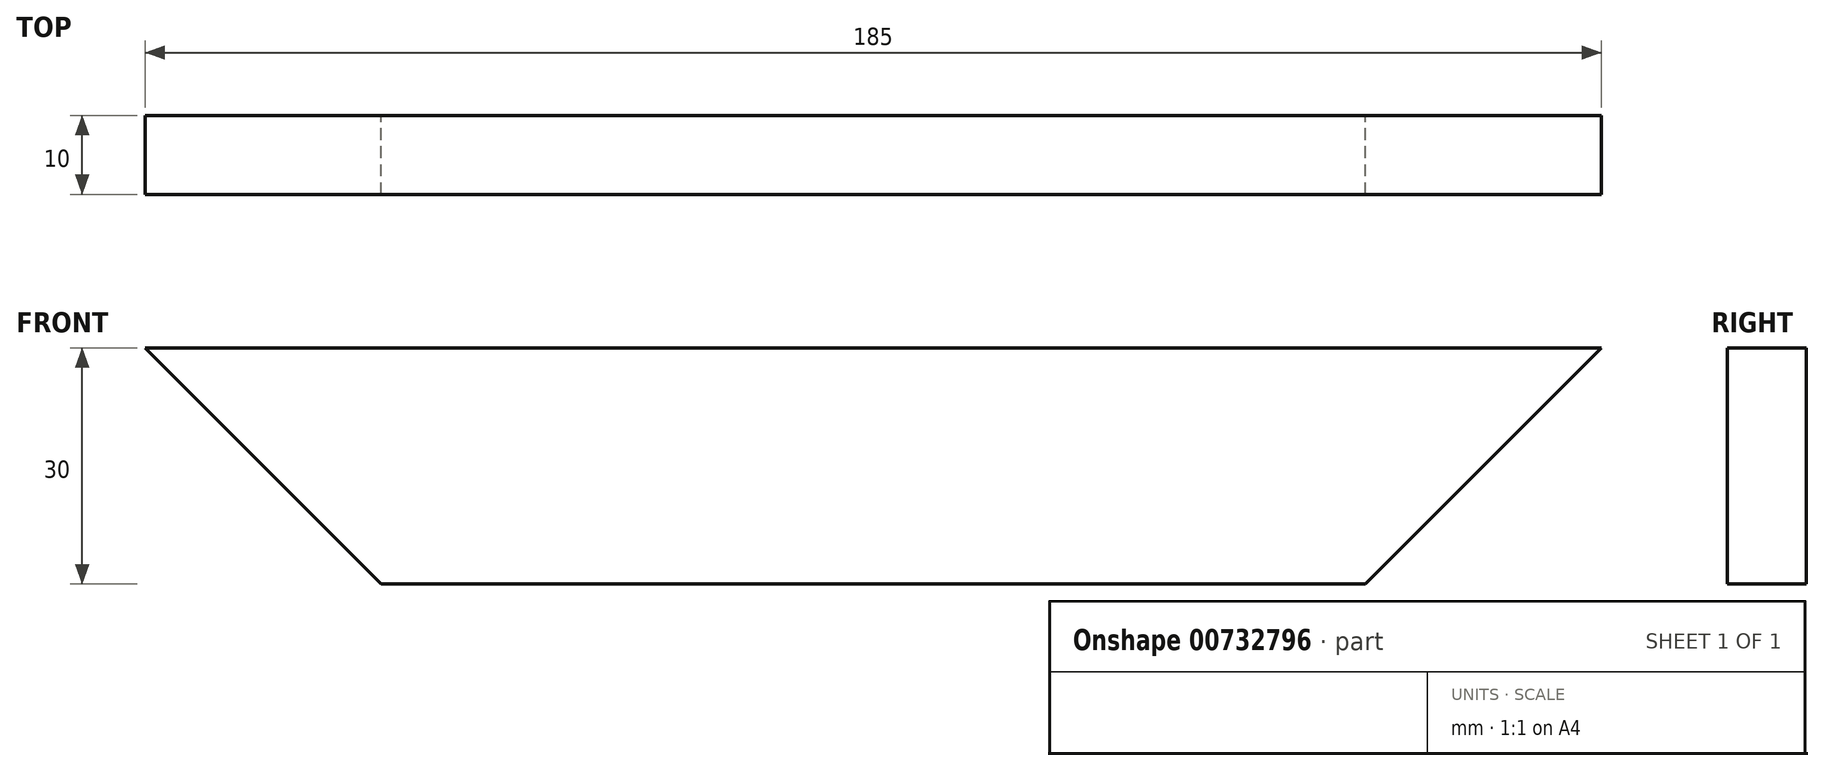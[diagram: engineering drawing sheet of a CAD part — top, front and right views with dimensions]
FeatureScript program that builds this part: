
annotation { "Feature Type Name" : "Feature", "Feature Type Description" : "" }
export const myFeature = defineFeature(function(context is Context, id is Id, definition is map)
    precondition{}
    {
        {
            var Q0;
            Q0=qCreatedBy(makeId("Front.planeOp"),FACE);
            var sketch = newSketch(context, id + "F0", { "sketchPlane" : qUnion([Q0])});
            skLineSegment(sketch, "E0", {"start": v(-138.14, -17.37) * mm, "end": v(-13.14, -17.37) * mm});
            skLineSegment(sketch, "E1", {"start": v(-13.14, -17.37) * mm, "end": v(16.86, 12.63) * mm});
            skLineSegment(sketch, "E2", {"start": v(16.86, 12.63) * mm, "end": v(-168.14, 12.63) * mm});
            skLineSegment(sketch, "E3", {"start": v(-168.14, 12.63) * mm, "end": v(-138.14, -17.37) * mm});
            skLineSegment(sketch, "E4", {"start": v(-138.14, -17.37) * mm, "end": v(-138.14, 12.63) * mm, "construction": true});
            skLineSegment(sketch, "E5", {"start": v(-13.14, -17.37) * mm, "end": v(-13.14, 12.63) * mm, "construction": true});
            skSolve(sketch);
        }
        {
            var Q0;
            Q0 = qSketchRegion(id + "F0", true);
            extrude(context, id + "F1", {"entities" : qUnion([Q0]), "depth" : 10 * mm, "offsetDistance" : 25 * mm});
        }
    });
